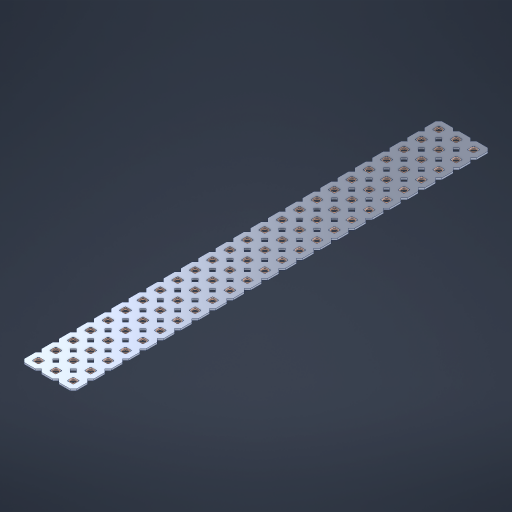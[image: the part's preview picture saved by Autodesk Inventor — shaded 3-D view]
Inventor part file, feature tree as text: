
AUTODESK INVENTOR PART (.ipt)
format: ipt  version: 2023 (Build 270158000, 158)  size: 1,093,120 bytes
history: native  units: in
note: dims shown in document units (in); Inventor stores cm internally (conversion verified against a paired STEP export)
features: other x73, extrude x71, sketch x2, pattern_linear x1
ambient origin geometry x8: Origin, YZ Plane, XZ Plane, XY Plane, X Axis, Y Axis, Z Axis, Center Point
bodies: Solid1 (feature_tree), Body (feature_tree)
feature tree (147):
  pattern_linear  "Rectangular Pattern1"  Spacing1=0.09in  [1 undecoded]
  sketch  "Sketch1"  dims[d1=0.5in]
  sketch  "Sketch2"  dims[d2=0.182in d3=0.09in d4=0.09in d5=0.09in d6=0.09in d7=0.09in d8=0.09in d9=0.09in d10=0.09in d11=0.02in d13=0.0in d14=0.172in d15=0.0625in d16=0.0in d19=0.5in d22=0.5in]
  other  "Srf1"
  other  "Srf126"
  other  "Srf127"
  other  "Srf128"
  other  "Srf129"
  other  "Srf130"
  other  "Srf131"
  other  "Srf250"
  other  "Srf251"
  other  "Srf252"
  other  "Srf253"
  other  "Srf254"
  other  "Srf255"
  other  "Srf256"
  other  "Srf257"
  other  "Srf258"
  other  "Srf259"
  other  "Srf260"
  other  "Srf261"
  other  "Srf262"
  other  "Srf263"
  other  "Srf264"
  other  "Srf265"
  other  "Srf266"
  other  "Srf268"
  other  "Srf269"
  other  "Srf270"
  other  "Srf271"
  other  "Srf272"
  other  "Srf273"
  other  "Srf274"
  other  "Srf275"
  other  "Srf276"
  other  "Srf277"
  other  "Srf278"
  other  "Srf279"
  other  "Srf280"
  other  "Srf281"
  other  "Srf282"
  other  "Srf283"
  other  "Srf284"
  other  "Srf285"
  other  "Srf286"
  other  "Srf287"
  other  "Srf288"
  other  "Srf289"
  other  "Srf290"
  other  "Srf291"
  other  "Srf293"
  other  "Srf294"
  other  "Srf295"
  other  "Srf296"
  other  "Srf297"
  other  "Srf298"
  other  "Srf299"
  other  "Srf300"
  other  "Srf301"
  other  "Srf302"
  other  "Srf303"
  other  "Srf304"
  other  "Srf305"
  other  "Srf306"
  other  "Srf307"
  other  "Srf308"
  other  "Srf309"
  other  "Srf310"
  other  "Srf311"
  other  "Srf312"
  other  "Srf313"
  other  "Srf314"
  other  "Srf315"
  other  "Srf316"
  other  "Circle"
  extrude  "ExtrusionSrf126"  Depth=0.09in
  extrude  "ExtrusionSrf127"  Depth=0.09in
  extrude  "ExtrusionSrf128"  Depth=0.09in
  extrude  "ExtrusionSrf129"  Depth=0.09in
  extrude  "ExtrusionSrf130"  Depth=0.09in
  extrude  "ExtrusionSrf131"  Depth=0.09in
  extrude  "ExtrusionSrf250"  Depth=0.09in
  extrude  "ExtrusionSrf251"  Depth=0.02in
  extrude  "ExtrusionSrf252"  TaperAngle=0.0deg  [1 undecoded]
  extrude  "ExtrusionSrf253"  Depth=0.5in
  extrude  "ExtrusionSrf254"  Depth=0.5in TaperAngle=0.0deg
  extrude  "ExtrusionSrf255"  Depth=0.5in
  extrude  "ExtrusionSrf256"  Depth=0.5in
  extrude  "ExtrusionSrf257"  [1 undecoded]
  extrude  "ExtrusionSrf258"  [1 undecoded]
  extrude  "ExtrusionSrf259"  [1 undecoded]
  extrude  "ExtrusionSrf260"  [1 undecoded]
  extrude  "ExtrusionSrf261"  [1 undecoded]
  extrude  "ExtrusionSrf262"  [1 undecoded]
  extrude  "ExtrusionSrf263"  [1 undecoded]
  extrude  "ExtrusionSrf264"  [1 undecoded]
  extrude  "ExtrusionSrf265"  [1 undecoded]
  extrude  "ExtrusionSrf266"  [1 undecoded]
  extrude  "ExtrusionSrf268"  [1 undecoded]
  extrude  "ExtrusionSrf269"  [1 undecoded]
  extrude  "ExtrusionSrf270"  [1 undecoded]
  extrude  "ExtrusionSrf271"  [1 undecoded]
  extrude  "ExtrusionSrf272"  [1 undecoded]
  extrude  "ExtrusionSrf273"  [1 undecoded]
  extrude  "ExtrusionSrf274"  [1 undecoded]
  extrude  "ExtrusionSrf275"  [1 undecoded]
  extrude  "ExtrusionSrf276"  [1 undecoded]
  extrude  "ExtrusionSrf277"  [1 undecoded]
  extrude  "ExtrusionSrf278"  [1 undecoded]
  extrude  "ExtrusionSrf279"  [1 undecoded]
  extrude  "ExtrusionSrf280"  [1 undecoded]
  extrude  "ExtrusionSrf281"  [1 undecoded]
  extrude  "ExtrusionSrf282"  [1 undecoded]
  extrude  "ExtrusionSrf283"  [1 undecoded]
  extrude  "ExtrusionSrf284"  [1 undecoded]
  extrude  "ExtrusionSrf285"  [1 undecoded]
  extrude  "ExtrusionSrf286"  [1 undecoded]
  extrude  "ExtrusionSrf287"  [1 undecoded]
  extrude  "ExtrusionSrf288"  [1 undecoded]
  extrude  "ExtrusionSrf289"  [1 undecoded]
  extrude  "ExtrusionSrf290"  [1 undecoded]
  extrude  "ExtrusionSrf291"  [1 undecoded]
  extrude  "ExtrusionSrf293"  [1 undecoded]
  extrude  "ExtrusionSrf294"  [1 undecoded]
  extrude  "ExtrusionSrf295"  [1 undecoded]
  extrude  "ExtrusionSrf296"  [1 undecoded]
  extrude  "ExtrusionSrf297"  [1 undecoded]
  extrude  "ExtrusionSrf298"  [1 undecoded]
  extrude  "ExtrusionSrf299"  [1 undecoded]
  extrude  "ExtrusionSrf300"  [1 undecoded]
  extrude  "ExtrusionSrf301"  [1 undecoded]
  extrude  "ExtrusionSrf302"  [1 undecoded]
  extrude  "ExtrusionSrf303"  [1 undecoded]
  extrude  "ExtrusionSrf304"  [1 undecoded]
  extrude  "ExtrusionSrf305"  [1 undecoded]
  extrude  "ExtrusionSrf306"  [1 undecoded]
  extrude  "ExtrusionSrf307"  [1 undecoded]
  extrude  "ExtrusionSrf308"  [1 undecoded]
  extrude  "ExtrusionSrf309"  [1 undecoded]
  extrude  "ExtrusionSrf310"  [1 undecoded]
  extrude  "ExtrusionSrf311"  [1 undecoded]
  extrude  "ExtrusionSrf312"  [1 undecoded]
  extrude  "ExtrusionSrf313"  [1 undecoded]
  extrude  "ExtrusionSrf314"  [1 undecoded]
  extrude  "ExtrusionSrf315"  [1 undecoded]
  extrude  "ExtrusionSrf316"  [1 undecoded]
note: 60 required parameter values undecoded (feature->parameter linkage not recoverable at this tier; creation-order binding heuristic only, values carry confidence <= 0.55)
